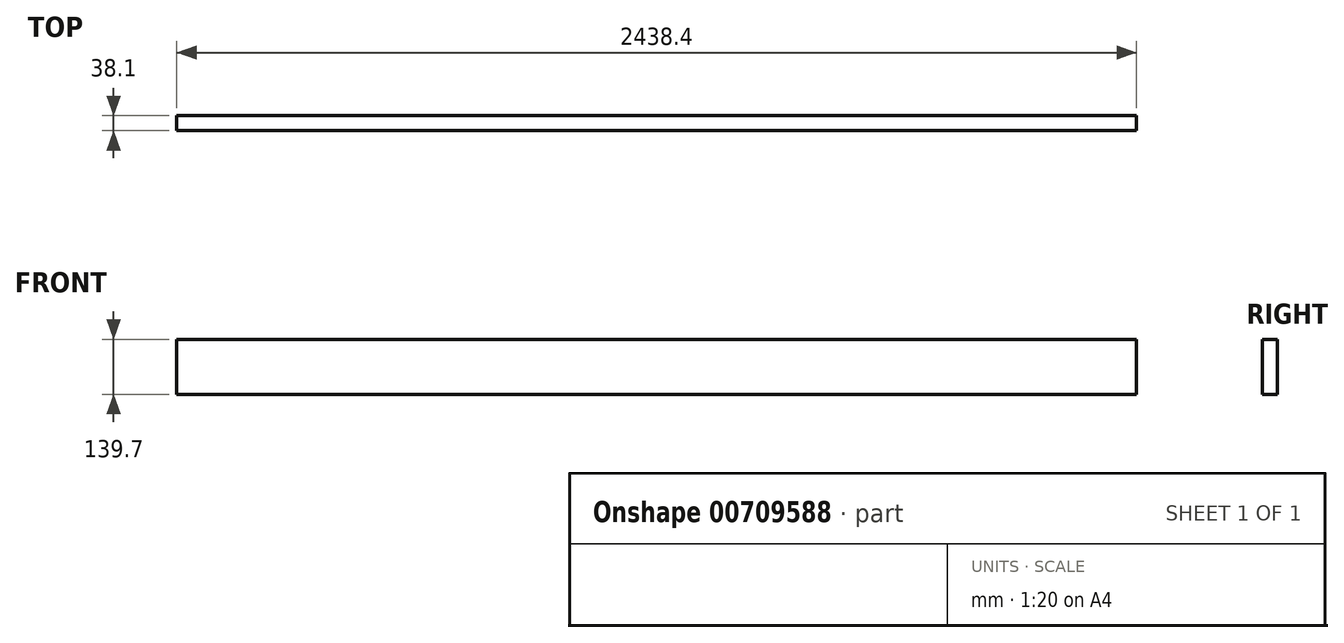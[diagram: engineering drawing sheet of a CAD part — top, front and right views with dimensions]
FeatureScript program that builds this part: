
annotation { "Feature Type Name" : "Feature", "Feature Type Description" : "" }
export const myFeature = defineFeature(function(context is Context, id is Id, definition is map)
    precondition{}
    {
        {
            var Q0;
            Q0=qCreatedBy(makeId("Front.planeOp"),FACE);
            var sketch = newSketch(context, id + "F0", { "sketchPlane" : qUnion([Q0])});
            skLineSegment(sketch, "E0.bottom", {"start": v(0, 0) * mm, "end": v(139.7, 0) * mm});
            skLineSegment(sketch, "E0.top", {"start": v(0, 2438.4) * mm, "end": v(139.7, 2438.4) * mm});
            skLineSegment(sketch, "E0.left", {"start": v(0, 0) * mm, "end": v(0, 2438.4) * mm});
            skLineSegment(sketch, "E0.right", {"start": v(139.7, 0) * mm, "end": v(139.7, 2438.4) * mm});
            skSolve(sketch);
        }
        {
            var Q0;
            Q0 = qSketchRegion(id + "F0", true);
            extrude(context, id + "F1", {"entities" : qUnion([Q0]), "depth" : 38.1 * mm, "offsetDistance" : 25.4 * mm});
        }
        {
            var Q0;
            Q0=makeQuery(id+"F1.opExtrude","SWEPT_BODY",BODY,{"disambiguationData":[OSD([sQuery(id+"F0.wireOp",EDGE,"E0.bottom"),sQuery(id+"F0.wireOp",EDGE,"E0.top"),sQuery(id+"F0.wireOp",EDGE,"E0.left"),sQuery(id+"F0.wireOp",EDGE,"E0.right")])]});
            var Q1;
            Q1=makeQuery(id+"F1.opExtrude","SWEPT_EDGE",EDGE,{"disambiguationData":[OSD([sQuery(id+"F0.wireOp",EDGE,"E0.bottom"),sQuery(id+"F0.wireOp",EDGE,"E0.right")])]});
            transform(context, id + "F2", {"entities" : qUnion([Q0]), "transformType" : TransformType.ROTATION, "transformAxis" : qUnion([Q1]), "angle" : 90 * degree, "makeCopy" : false});
        }
    });
